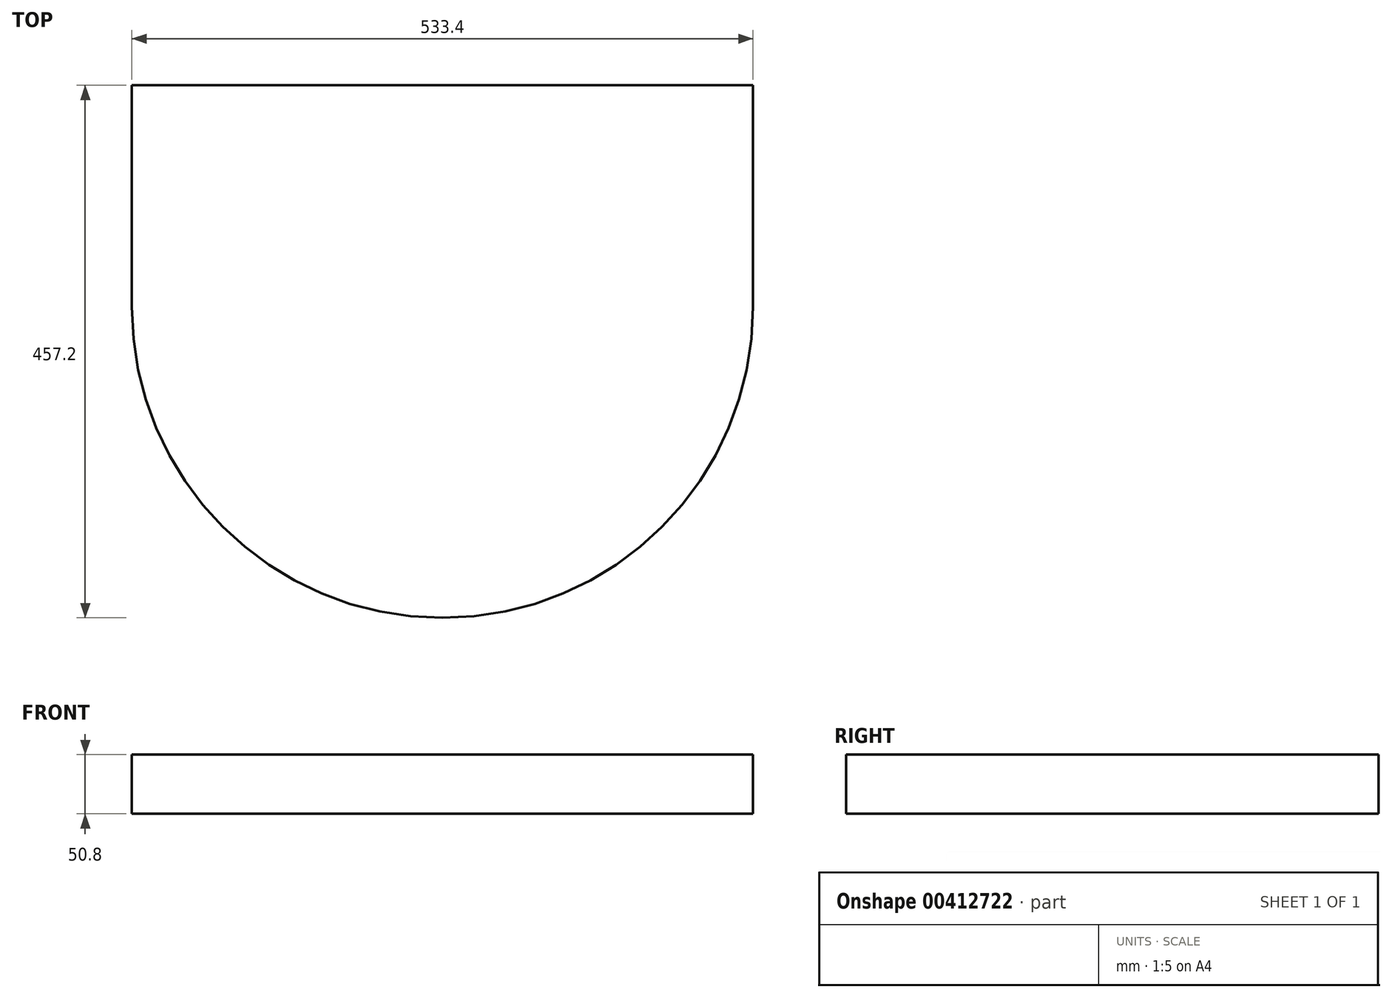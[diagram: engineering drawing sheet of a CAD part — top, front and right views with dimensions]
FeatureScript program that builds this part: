
annotation { "Feature Type Name" : "Feature", "Feature Type Description" : "" }
export const myFeature = defineFeature(function(context is Context, id is Id, definition is map)
    precondition{}
    {
        {
            var Q0;
            Q0=qCreatedBy(makeId("Top.planeOp"),FACE);
            var sketch = newSketch(context, id + "F0", { "sketchPlane" : qUnion([Q0])});
            skLineSegment(sketch, "E0.bottom", {"start": v(266.7, 228.6) * mm, "end": v(-266.7, 228.6) * mm});
            skLineSegment(sketch, "E0.top", {"start": v(266.7, -228.6) * mm, "end": v(-266.7, -228.6) * mm});
            skLineSegment(sketch, "E0.left", {"start": v(266.7, 228.6) * mm, "end": v(266.7, -228.6) * mm});
            skLineSegment(sketch, "E0.right", {"start": v(-266.7, 228.6) * mm, "end": v(-266.7, -228.6) * mm});
            skPoint(sketch, "E0.middle", {"position": v(0, 0) * mm});
            skArc(sketch, "E1", {"start": v(-266.7, 38.1) * mm, "mid": v(0, -228.6) * mm, "end": v(266.7, 38.1) * mm});
            skSolve(sketch);
        }
        {
            var Q0;
            {var subQ5=sQuery(id+"F0.wireOp",EDGE,"E0.bottom");Q0=makeQuery(id+"F0.imprint","IMPRINT",FACE,{"disambiguationData":[TD([[makeQuery(id+"F0.imprint","IMPRINT",EDGE,{"derivedFrom":subQ5}),1.0]])]});}
            extrude(context, id + "F1", {"entities" : qUnion([Q0]), "endBound" : BoundingType.SYMMETRIC, "depth" : 50.8 * mm});
        }
    });
